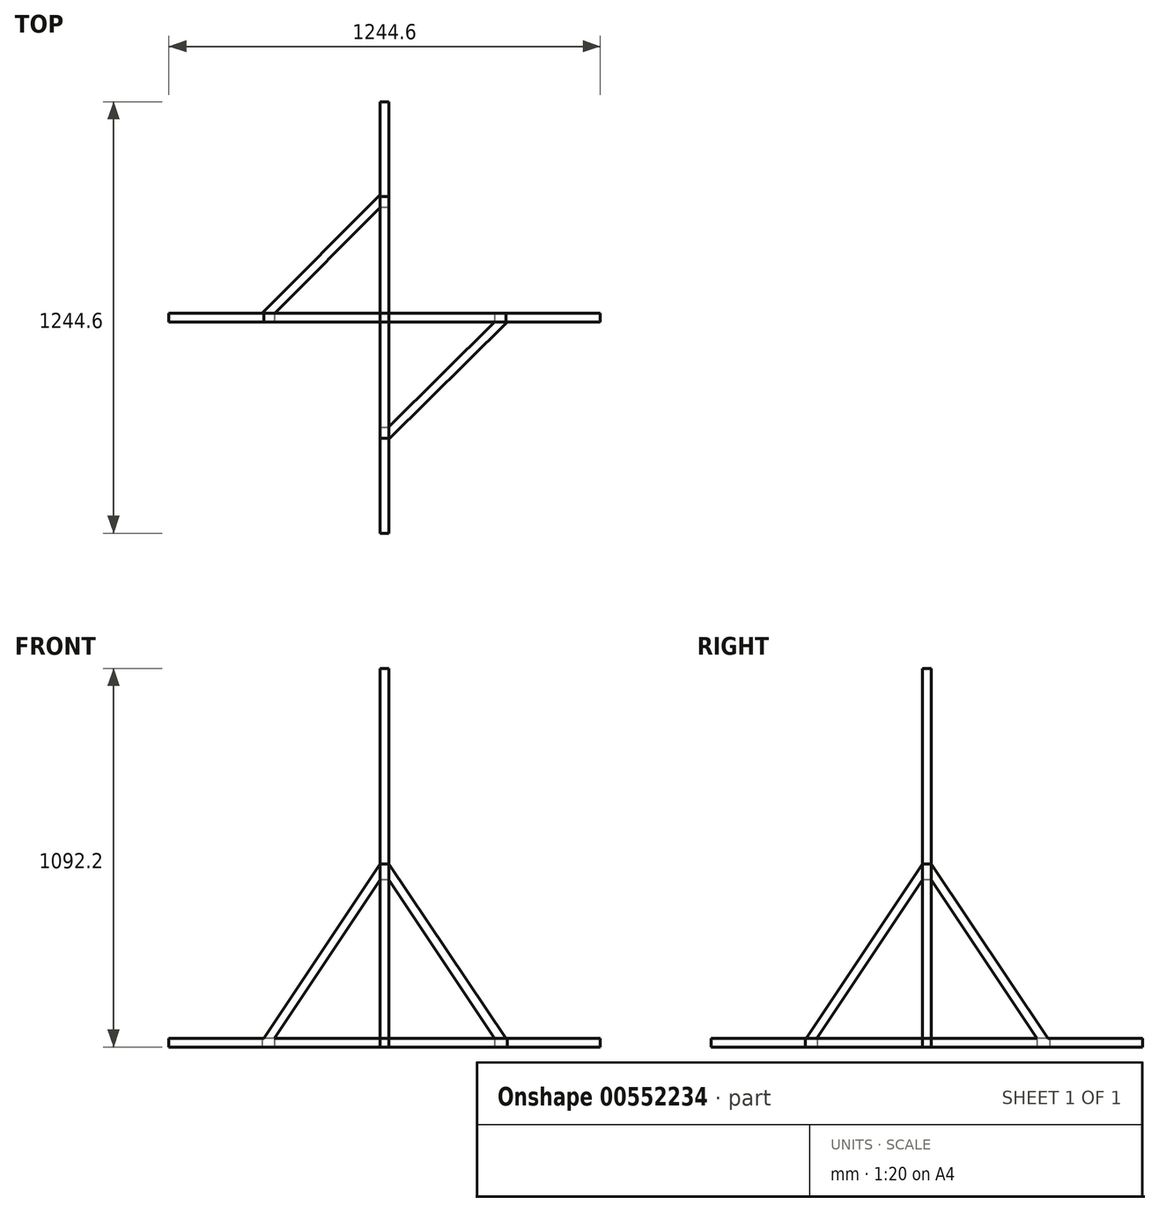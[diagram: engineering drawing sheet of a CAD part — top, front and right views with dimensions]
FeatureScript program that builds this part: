
annotation { "Feature Type Name" : "Feature", "Feature Type Description" : "" }
export const myFeature = defineFeature(function(context is Context, id is Id, definition is map)
    precondition{}
    {
        {
            var Q0;
            Q0=qCreatedBy(makeId("Front.planeOp"),FACE);
            var sketch = newSketch(context, id + "F0", { "sketchPlane" : qUnion([Q0])});
            skLineSegment(sketch, "E0.bottom", {"start": v(-12.7, 12.7) * mm, "end": v(12.7, 12.7) * mm});
            skLineSegment(sketch, "E0.top", {"start": v(-12.7, -12.7) * mm, "end": v(12.7, -12.7) * mm});
            skLineSegment(sketch, "E0.left", {"start": v(-12.7, 12.7) * mm, "end": v(-12.7, -12.7) * mm});
            skLineSegment(sketch, "E0.right", {"start": v(12.7, 12.7) * mm, "end": v(12.7, -12.7) * mm});
            skPoint(sketch, "E0.middle", {"position": v(0, 0) * mm});
            skSolve(sketch);
        }
        {
            var Q0;
            Q0 = qSketchRegion(id + "F0", true);
            extrude(context, id + "F1", {"entities" : qUnion([Q0]), "depth" : 622.3 * mm, "offsetDistance" : 25.4 * mm});
        }
        {
            var Q0;
            Q0=qCreatedBy(makeId("Front.planeOp"),FACE);
            var sketch = newSketch(context, id + "F2", { "sketchPlane" : qUnion([Q0])});
            skLineSegment(sketch, "E1.bottom", {"start": v(-12.7, -12.7) * mm, "end": v(12.7, -12.7) * mm});
            skLineSegment(sketch, "E1.top", {"start": v(-12.7, 12.7) * mm, "end": v(12.7, 12.7) * mm});
            skLineSegment(sketch, "E1.left", {"start": v(-12.7, -12.7) * mm, "end": v(-12.7, 12.7) * mm});
            skLineSegment(sketch, "E1.right", {"start": v(12.7, -12.7) * mm, "end": v(12.7, 12.7) * mm});
            skPoint(sketch, "E1.middle", {"position": v(0, 0) * mm});
            skSolve(sketch);
        }
        {
            var Q0;
            Q0 = qSketchRegion(id + "F2", true);
            extrude(context, id + "F3", {"entities" : qUnion([Q0]), "operationType" : NewBodyOperationType.ADD, "oppositeDirection" : true, "depth" : 622.3 * mm, "offsetDistance" : 25.4 * mm});
        }
        {
            var Q0;
            Q0=qCreatedBy(makeId("Top.planeOp"),FACE);
            var sketch = newSketch(context, id + "F4", { "sketchPlane" : qUnion([Q0])});
            skLineSegment(sketch, "E2.bottom", {"start": v(-12.7, 12.7) * mm, "end": v(12.7, 12.7) * mm});
            skLineSegment(sketch, "E2.top", {"start": v(-12.7, -12.7) * mm, "end": v(12.7, -12.7) * mm});
            skLineSegment(sketch, "E2.left", {"start": v(-12.7, 12.7) * mm, "end": v(-12.7, -12.7) * mm});
            skLineSegment(sketch, "E2.right", {"start": v(12.7, 12.7) * mm, "end": v(12.7, -12.7) * mm});
            skPoint(sketch, "E2.middle", {"position": v(0, 0) * mm});
            skSolve(sketch);
        }
        {
            var Q0;
            Q0 = qSketchRegion(id + "F4", true);
            extrude(context, id + "F5", {"entities" : qUnion([Q0]), "operationType" : NewBodyOperationType.ADD, "depth" : 622.3 * mm, "offsetDistance" : 25.4 * mm});
        }
        {
            var Q0;
            Q0=qCreatedBy(makeId("Top.planeOp"),FACE);
            var sketch = newSketch(context, id + "F6", { "sketchPlane" : qUnion([Q0])});
            skLineSegment(sketch, "E3.bottom", {"start": v(12.7, 12.7) * mm, "end": v(-12.7, 12.7) * mm});
            skLineSegment(sketch, "E3.top", {"start": v(12.7, -12.7) * mm, "end": v(-12.7, -12.7) * mm});
            skLineSegment(sketch, "E3.left", {"start": v(12.7, 12.7) * mm, "end": v(12.7, -12.7) * mm});
            skLineSegment(sketch, "E3.right", {"start": v(-12.7, 12.7) * mm, "end": v(-12.7, -12.7) * mm});
            skPoint(sketch, "E3.middle", {"position": v(0, 0) * mm});
            skSolve(sketch);
        }
        {
            var Q0;
            Q0 = qSketchRegion(id + "F6", true);
            extrude(context, id + "F7", {"entities" : qUnion([Q0]), "operationType" : NewBodyOperationType.ADD, "oppositeDirection" : true, "depth" : 622.3 * mm, "offsetDistance" : 25.4 * mm});
        }
        {
            var Q0;
            Q0=qCreatedBy(makeId("Right.planeOp"),FACE);
            var sketch = newSketch(context, id + "F8", { "sketchPlane" : qUnion([Q0])});
            skPoint(sketch, "E4.middle", {"position": v(0, 0) * mm});
            skLineSegment(sketch, "E5", {"start": v(317.49, 10.18) * mm, "end": v(12.7, 317.5) * mm});
            skLineSegment(sketch, "E6", {"start": v(317.49, 10.18) * mm, "end": v(353.26, 10.18) * mm});
            skLineSegment(sketch, "E7", {"start": v(12.7, 317.5) * mm, "end": v(12.7, 353.57) * mm});
            skLineSegment(sketch, "E8", {"start": v(353.26, 10.18) * mm, "end": v(12.7, 353.57) * mm});
            skLineSegment(sketch, "E9", {"start": v(-317.5, -12.7) * mm, "end": v(-12.7, -317.5) * mm});
            skLineSegment(sketch, "E10", {"start": v(-12.7, -317.5) * mm, "end": v(-12.7, -353.42) * mm});
            skLineSegment(sketch, "E11", {"start": v(-317.5, -12.7) * mm, "end": v(-353.42, -12.7) * mm});
            skLineSegment(sketch, "E12", {"start": v(-353.42, -12.7) * mm, "end": v(-12.7, -353.42) * mm});
            skPoint(sketch, "E13.middle", {"position": v(-0.4, -0.9) * mm});
            skPoint(sketch, "E14.middle", {"position": v(0.04, 0.6) * mm});
            skLineSegment(sketch, "E15", {"start": v(317.53, 10.77) * mm, "end": v(12.74, 318.1) * mm});
            skLineSegment(sketch, "E16", {"start": v(317.53, 10.77) * mm, "end": v(353.3, 10.77) * mm});
            skLineSegment(sketch, "E17", {"start": v(12.74, 318.1) * mm, "end": v(12.74, 354.16) * mm});
            skLineSegment(sketch, "E18", {"start": v(353.3, 10.77) * mm, "end": v(12.74, 354.16) * mm});
            skLineSegment(sketch, "E19", {"start": v(-317.46, -12.1) * mm, "end": v(-12.66, -316.9) * mm});
            skLineSegment(sketch, "E20", {"start": v(-12.66, -316.9) * mm, "end": v(-12.66, -352.83) * mm});
            skLineSegment(sketch, "E21", {"start": v(-317.46, -12.1) * mm, "end": v(-353.38, -12.1) * mm});
            skLineSegment(sketch, "E22", {"start": v(-353.38, -12.1) * mm, "end": v(-12.66, -352.83) * mm});
            skSolve(sketch);
        }
        {
            var Q0;
            Q0 = qSketchRegion(id + "F8", true);
            extrude(context, id + "F9", {"entities" : qUnion([Q0]), "operationType" : NewBodyOperationType.ADD, "depth" : 12.7 * mm, "offsetDistance" : 25.4 * mm});
        }
        {
            var Q0;
            Q0 = qSketchRegion(id + "F8", true);
            extrude(context, id + "F10", {"entities" : qUnion([Q0]), "operationType" : NewBodyOperationType.ADD, "oppositeDirection" : true, "depth" : 12.7 * mm, "offsetDistance" : 25.4 * mm});
        }
        {
            var Q0;
            Q0=qCreatedBy(makeId("Right.planeOp"),FACE);
            var sketch = newSketch(context, id + "F11", { "sketchPlane" : qUnion([Q0])});
            skLineSegment(sketch, "E23.bottom", {"start": v(12.7, -12.7) * mm, "end": v(-12.7, -12.7) * mm});
            skLineSegment(sketch, "E23.top", {"start": v(12.7, 12.7) * mm, "end": v(-12.7, 12.7) * mm});
            skLineSegment(sketch, "E23.left", {"start": v(12.7, -12.7) * mm, "end": v(12.7, 12.7) * mm});
            skLineSegment(sketch, "E23.right", {"start": v(-12.7, -12.7) * mm, "end": v(-12.7, 12.7) * mm});
            skPoint(sketch, "E23.middle", {"position": v(0, 0) * mm});
            skSolve(sketch);
        }
        {
            var Q0;
            Q0 = qSketchRegion(id + "F11", true);
            extrude(context, id + "F12", {"entities" : qUnion([Q0]), "operationType" : NewBodyOperationType.ADD, "depth" : 1079.5 * mm, "offsetDistance" : 25.4 * mm});
        }
        {
            var Q0;
            Q0=qCreatedBy(makeId("Front.planeOp"),FACE);
            var sketch = newSketch(context, id + "F13", { "sketchPlane" : qUnion([Q0])});
            skPoint(sketch, "E24.middle", {"position": v(0, 0) * mm});
            skLineSegment(sketch, "E25", {"start": v(12.7, 317.5) * mm, "end": v(469.9, 12.7) * mm});
            skLineSegment(sketch, "E26", {"start": v(12.7, 349.3) * mm, "end": v(12.7, 317.5) * mm});
            skLineSegment(sketch, "E27", {"start": v(515.7, 12.7) * mm, "end": v(469.9, 12.7) * mm});
            skLineSegment(sketch, "E28", {"start": v(12.7, 349.3) * mm, "end": v(515.7, 12.7) * mm});
            skLineSegment(sketch, "E29", {"start": v(469.9, -12.7) * mm, "end": v(12.7, -317.5) * mm});
            skLineSegment(sketch, "E30", {"start": v(12.7, -317.5) * mm, "end": v(12.7, -348.03) * mm});
            skLineSegment(sketch, "E31", {"start": v(469.9, -12.7) * mm, "end": v(515.7, -12.7) * mm});
            skLineSegment(sketch, "E32", {"start": v(515.7, -12.7) * mm, "end": v(12.7, -348.03) * mm});
            skSolve(sketch);
        }
        {
            var Q0;
            Q0 = qSketchRegion(id + "F13", true);
            extrude(context, id + "F14", {"entities" : qUnion([Q0]), "operationType" : NewBodyOperationType.ADD, "depth" : 12.7 * mm, "offsetDistance" : 25.4 * mm});
        }
        {
            var Q0;
            Q0 = qSketchRegion(id + "F13", true);
            extrude(context, id + "F15", {"entities" : qUnion([Q0]), "operationType" : NewBodyOperationType.ADD, "oppositeDirection" : true, "depth" : 12.7 * mm, "offsetDistance" : 25.4 * mm});
        }
        {
            var Q0;
            Q0=qCreatedBy(makeId("Top.planeOp"),FACE);
            var sketch = newSketch(context, id + "F16", { "sketchPlane" : qUnion([Q0])});
            skPoint(sketch, "E33.middle", {"position": v(0, 0) * mm});
            skLineSegment(sketch, "E34", {"start": v(469.9, 12.7) * mm, "end": v(12.7, 317.5) * mm});
            skLineSegment(sketch, "E35", {"start": v(469.9, -12.7) * mm, "end": v(12.7, -317.5) * mm});
            skLineSegment(sketch, "E36", {"start": v(12.7, -348.03) * mm, "end": v(12.7, -317.5) * mm});
            skLineSegment(sketch, "E37", {"start": v(515.7, -12.7) * mm, "end": v(469.9, -12.7) * mm});
            skLineSegment(sketch, "E38", {"start": v(515.7, -12.7) * mm, "end": v(12.7, -348.03) * mm});
            skLineSegment(sketch, "E39", {"start": v(515.7, 12.7) * mm, "end": v(469.9, 12.7) * mm});
            skLineSegment(sketch, "E40", {"start": v(12.7, 317.5) * mm, "end": v(12.7, 348.03) * mm});
            skLineSegment(sketch, "E41", {"start": v(515.7, 12.7) * mm, "end": v(12.7, 348.03) * mm});
            skSolve(sketch);
        }
        {
            var Q0;
            Q0 = qSketchRegion(id + "F16", true);
            extrude(context, id + "F17", {"entities" : qUnion([Q0]), "operationType" : NewBodyOperationType.ADD, "depth" : 12.7 * mm, "offsetDistance" : 25.4 * mm});
        }
        {
            var Q0;
            Q0 = qSketchRegion(id + "F16", true);
            extrude(context, id + "F18", {"entities" : qUnion([Q0]), "operationType" : NewBodyOperationType.ADD, "oppositeDirection" : true, "depth" : 12.7 * mm, "offsetDistance" : 25.4 * mm});
        }
        {
            var Q0;
            Q0=makeQuery(id+"F1.opExtrude","SWEPT_BODY",BODY,{"disambiguationData":[OSD([sQuery(id+"F0.wireOp",EDGE,"E0.bottom"),sQuery(id+"F0.wireOp",EDGE,"E0.top"),sQuery(id+"F0.wireOp",EDGE,"E0.left"),sQuery(id+"F0.wireOp",EDGE,"E0.right")])]});
            var Q1;
            {var subQ0=sQuery(id+"F2.wireOp",EDGE,"E1.left");var subQ1=sQuery(id+"F2.wireOp",EDGE,"E1.bottom");var subQ2=sQuery(id+"F0.wireOp",EDGE,"E0.top");var subQ3=sQuery(id+"F0.wireOp",EDGE,"E0.left");Q1=makeQuery(id+"F7.boolean.opBoolean","SPLIT",EDGE,{"disambiguationData":[TD([makeQuery(id+"F7.opExtrude","SWEPT_FACE",FACE,{"disambiguationData":[OSD([sQuery(id+"F6.wireOp",EDGE,"E3.bottom")])]})])],"derivedFrom":makeQuery(id+"F3.boolean.opBoolean","MERGE",EDGE,{"derivedFrom":[makeQuery(id+"F1.opExtrude","SWEPT_EDGE",EDGE,{"disambiguationData":[OSD([subQ2,subQ3])]}),makeQuery(id+"F3.opExtrude","SWEPT_EDGE",EDGE,{"disambiguationData":[OSD([subQ1,subQ0])]})]})});}
            transform(context, id + "F19", {"entities" : qUnion([Q0]), "transformType" : TransformType.ROTATION, "transformAxis" : qUnion([Q1]), "angle" : 90 * degree, "makeCopy" : false});
        }
        {
            var Q0;
            Q0=makeQuery(id+"F1.opExtrude","SWEPT_BODY",BODY,{"disambiguationData":[OSD([sQuery(id+"F0.wireOp",EDGE,"E0.bottom"),sQuery(id+"F0.wireOp",EDGE,"E0.top"),sQuery(id+"F0.wireOp",EDGE,"E0.left"),sQuery(id+"F0.wireOp",EDGE,"E0.right")])]});
            var Q1;
            {var subQ0=sQuery(id+"F11.wireOp",EDGE,"E23.bottom");var subQ1=sQuery(id+"F11.wireOp",EDGE,"E23.left");Q1=makeQuery(id+"F15.boolean.opBoolean","SPLIT",EDGE,{"disambiguationData":[TD([makeQuery(id+"F1.opExtrude","SWEPT_FACE",FACE,{"disambiguationData":[OSD([sQuery(id+"F0.wireOp",EDGE,"E0.top")])]})])],"derivedFrom":makeQuery(id+"F12.opExtrude","SWEPT_EDGE",EDGE,{"disambiguationData":[OSD([subQ0,subQ1])]})});}
            transform(context, id + "F20", {"entities" : qUnion([Q0]), "transformType" : TransformType.TRANSLATION_DISTANCE, "transformDirection" : qUnion([Q1]), "distance" : 25.4 * mm, "makeCopy" : false});
        }
        {
            var Q0;
            Q0=makeQuery(id+"F1.opExtrude","SWEPT_BODY",BODY,{"disambiguationData":[OSD([sQuery(id+"F0.wireOp",EDGE,"E0.bottom"),sQuery(id+"F0.wireOp",EDGE,"E0.top"),sQuery(id+"F0.wireOp",EDGE,"E0.left"),sQuery(id+"F0.wireOp",EDGE,"E0.right")])]});
            var Q1;
            Q1=makeQuery(id+"F7.opExtrude","SWEPT_EDGE",EDGE,{"disambiguationData":[OSD([sQuery(id+"F6.wireOp",EDGE,"E3.bottom"),sQuery(id+"F6.wireOp",EDGE,"E3.right")])]});
            transform(context, id + "F21", {"entities" : qUnion([Q0]), "transformType" : TransformType.ROTATION, "transformAxis" : qUnion([Q1]), "angle" : 180 * degree, "makeCopy" : false});
        }
        {
            var Q0;
            Q0=makeQuery(id+"F1.opExtrude","SWEPT_BODY",BODY,{"disambiguationData":[OSD([sQuery(id+"F0.wireOp",EDGE,"E0.bottom"),sQuery(id+"F0.wireOp",EDGE,"E0.top"),sQuery(id+"F0.wireOp",EDGE,"E0.left"),sQuery(id+"F0.wireOp",EDGE,"E0.right")])]});
            var Q1;
            {var subQ0=sQuery(id+"F2.wireOp",EDGE,"E1.right");var subQ2=makeQuery(id+"F5.opExtrude","SWEPT_FACE",FACE,{"disambiguationData":[OSD([sQuery(id+"F4.wireOp",EDGE,"E2.bottom")])]});var subQ3=sQuery(id+"F2.wireOp",EDGE,"E1.top");var subQ5=sQuery(id+"F0.wireOp",EDGE,"E0.right");var subQ8=sQuery(id+"F0.wireOp",EDGE,"E0.bottom");Q1=makeQuery(id+"F9.boolean.opBoolean","SPLIT",EDGE,{"disambiguationData":[TD([subQ2])],"derivedFrom":makeQuery(id+"F5.boolean.opBoolean","SPLIT",EDGE,{"disambiguationData":[TD([subQ2])],"derivedFrom":makeQuery(id+"F3.boolean.opBoolean","MERGE",EDGE,{"derivedFrom":[makeQuery(id+"F1.opExtrude","SWEPT_EDGE",EDGE,{"disambiguationData":[OSD([subQ8,subQ5])]}),makeQuery(id+"F3.opExtrude","SWEPT_EDGE",EDGE,{"disambiguationData":[OSD([subQ3,subQ0])]})]})})});}
            transform(context, id + "F22", {"entities" : qUnion([Q0]), "transformType" : TransformType.TRANSLATION_DISTANCE, "transformDirection" : qUnion([Q1]), "distance" : 25.4 * mm, "makeCopy" : false});
        }
        {
            var Q0;
            Q0=makeQuery(id+"F1.opExtrude","SWEPT_BODY",BODY,{"disambiguationData":[OSD([sQuery(id+"F0.wireOp",EDGE,"E0.bottom"),sQuery(id+"F0.wireOp",EDGE,"E0.top"),sQuery(id+"F0.wireOp",EDGE,"E0.left"),sQuery(id+"F0.wireOp",EDGE,"E0.right")])]});
            var Q1;
            {var subQ0=sQuery(id+"F11.wireOp",EDGE,"E23.left");var subQ1=sQuery(id+"F11.wireOp",EDGE,"E23.top");Q1=makeQuery(id+"F15.boolean.opBoolean","SPLIT",EDGE,{"disambiguationData":[TD([makeQuery(id+"F1.opExtrude","SWEPT_FACE",FACE,{"disambiguationData":[OSD([sQuery(id+"F0.wireOp",EDGE,"E0.bottom")])]})])],"derivedFrom":makeQuery(id+"F12.opExtrude","SWEPT_EDGE",EDGE,{"disambiguationData":[OSD([subQ1,subQ0])]})});}
            transform(context, id + "F23", {"entities" : qUnion([Q0]), "transformType" : TransformType.TRANSLATION_DISTANCE, "transformDirection" : qUnion([Q1]), "distance" : 25.4 * mm, "makeCopy" : false});
        }
    });
